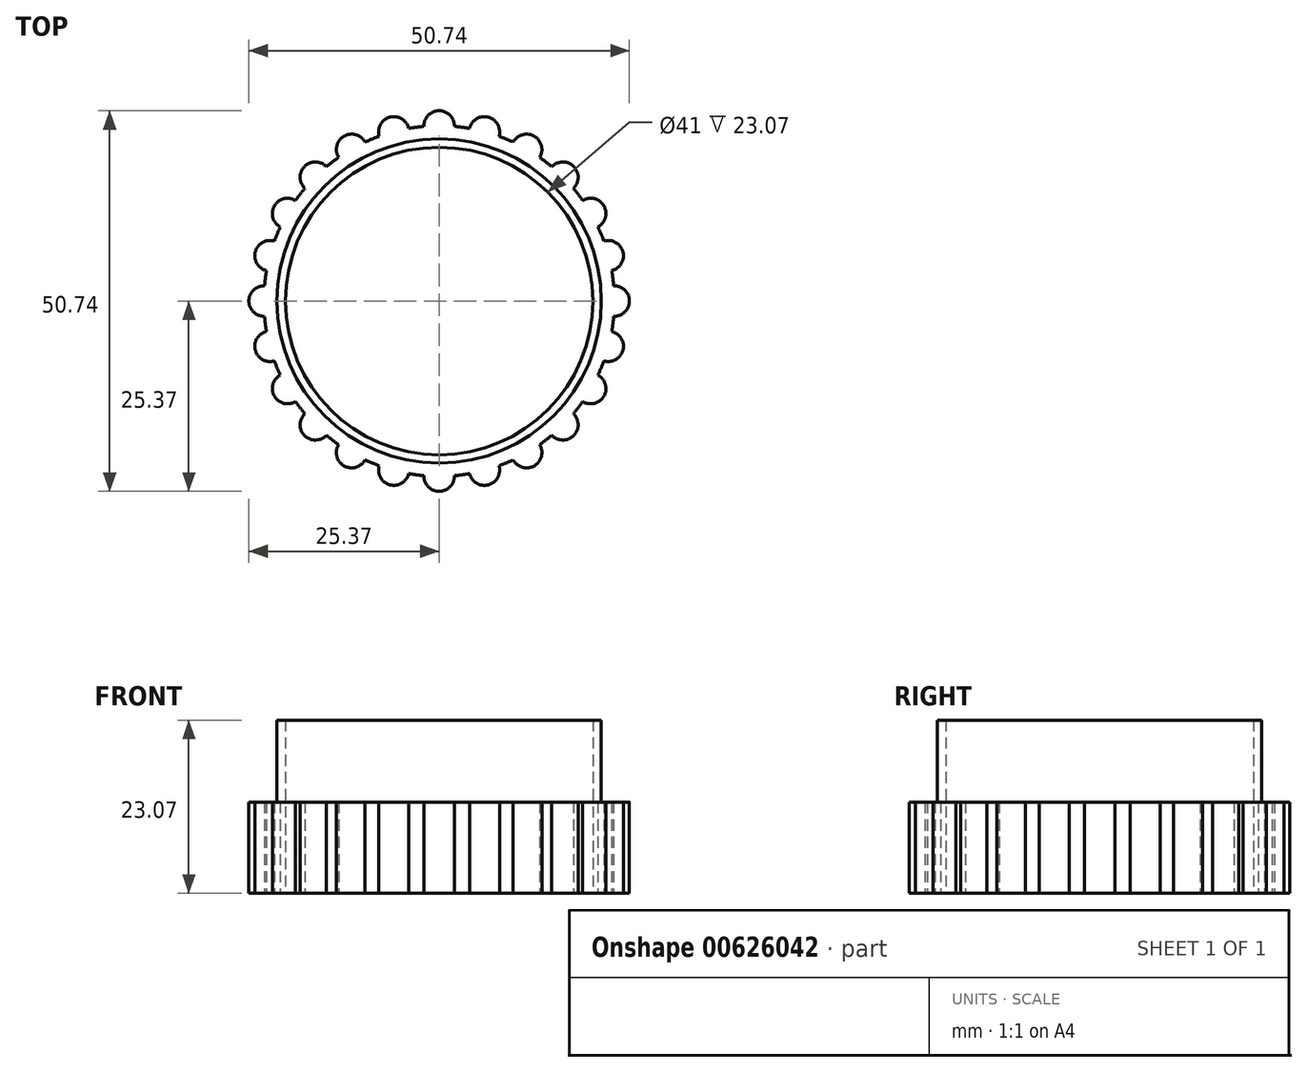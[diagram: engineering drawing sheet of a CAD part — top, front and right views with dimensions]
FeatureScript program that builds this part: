
annotation { "Feature Type Name" : "Feature", "Feature Type Description" : "" }
export const myFeature = defineFeature(function(context is Context, id is Id, definition is map)
    precondition{}
    {
        {
            var Q0;
            Q0=qCreatedBy(makeId("Front.planeOp"),FACE);
            var sketch = newSketch(context, id + "F0", { "sketchPlane" : qUnion([Q0])});
            skLineSegment(sketch, "E0", {"start": v(20.5, 0) * mm, "end": v(20.5, 23.07) * mm});
            skLineSegment(sketch, "E1", {"start": v(20.5, 23.07) * mm, "end": v(21.62, 23.07) * mm});
            skLineSegment(sketch, "E2", {"start": v(21.62, 23.07) * mm, "end": v(21.62, 12.13) * mm});
            skLineSegment(sketch, "E3", {"start": v(21.62, 12.13) * mm, "end": v(23.37, 12.13) * mm});
            skLineSegment(sketch, "E4", {"start": v(23.37, 12.13) * mm, "end": v(23.37, 0) * mm});
            skLineSegment(sketch, "E5", {"start": v(23.37, 0) * mm, "end": v(20.5, 0) * mm});
            skLineSegment(sketch, "E6", {"start": v(0, 0) * mm, "end": v(0, 12.84) * mm, "construction": true});
            skSolve(sketch);
        }
        {
            var Q0;
            Q0 = qSketchRegion(id + "F0", true);
            var Q1;
            Q1=sQuery(id+"F0.wireOp",EDGE,"E6");
            revolve(context, id + "F1", {"surfaceOperationType" : NewSurfaceOperationType.NEW, "entities" : qUnion([Q0]), "axis" : qUnion([Q1]), "revolveType" : RevolveType.FULL});
        }
        {
            var Q0;
            Q0=makeQuery(id+"F1.opRevolve","SWEPT_FACE",FACE,{"disambiguationData":[OSD([sQuery(id+"F0.wireOp",EDGE,"E5")])]});
            var sketch = newSketch(context, id + "F2", { "sketchPlane" : qUnion([Q0])});
            skCircle(sketch, "E7.0", {"center": v(0, 0) * mm, "radius": 23.37 * mm});
            skArc(sketch, "E8", {"start": v(2.03, 23.28) * mm, "mid": v(0, 25.37) * mm, "end": v(-2.03, 23.28) * mm});
            skArc(sketch, "E9.1.0", {"start": v(-4.06, 23.01) * mm, "mid": v(-6.57, 24.5) * mm, "end": v(-8, 21.96) * mm});
            skArc(sketch, "E9.2.0", {"start": v(-9.88, 21.18) * mm, "mid": v(-12.68, 21.97) * mm, "end": v(-13.4, 19.14) * mm});
            skArc(sketch, "E9.3.0", {"start": v(-15.02, 17.9) * mm, "mid": v(-17.94, 17.94) * mm, "end": v(-17.9, 15.02) * mm});
            skArc(sketch, "E9.4.0", {"start": v(-19.14, 13.4) * mm, "mid": v(-21.97, 12.68) * mm, "end": v(-21.18, 9.88) * mm});
            skArc(sketch, "E9.5.0", {"start": v(-21.96, 8) * mm, "mid": v(-24.5, 6.57) * mm, "end": v(-23.01, 4.06) * mm});
            skArc(sketch, "E9.6.0", {"start": v(-23.28, 2.04) * mm, "mid": v(-25.37, 0) * mm, "end": v(-23.28, -2.03) * mm});
            skArc(sketch, "E9.7.0", {"start": v(-23.01, -4.06) * mm, "mid": v(-24.5, -6.57) * mm, "end": v(-21.96, -8) * mm});
            skArc(sketch, "E9.8.0", {"start": v(-21.18, -9.88) * mm, "mid": v(-21.97, -12.68) * mm, "end": v(-19.14, -13.4) * mm});
            skArc(sketch, "E9.9.0", {"start": v(-17.9, -15.02) * mm, "mid": v(-17.94, -17.94) * mm, "end": v(-15.02, -17.9) * mm});
            skArc(sketch, "E9.10.0", {"start": v(-13.4, -19.14) * mm, "mid": v(-12.68, -21.97) * mm, "end": v(-9.88, -21.18) * mm});
            skArc(sketch, "E9.11.0", {"start": v(-8, -21.96) * mm, "mid": v(-6.57, -24.5) * mm, "end": v(-4.06, -23.01) * mm});
            skArc(sketch, "E9.12.0", {"start": v(-2.04, -23.28) * mm, "mid": v(0, -25.37) * mm, "end": v(2.03, -23.28) * mm});
            skArc(sketch, "E9.13.0", {"start": v(4.06, -23.01) * mm, "mid": v(6.57, -24.5) * mm, "end": v(8, -21.96) * mm});
            skArc(sketch, "E9.14.0", {"start": v(9.88, -21.18) * mm, "mid": v(12.68, -21.97) * mm, "end": v(13.4, -19.14) * mm});
            skArc(sketch, "E9.15.0", {"start": v(15.02, -17.9) * mm, "mid": v(17.94, -17.94) * mm, "end": v(17.9, -15.02) * mm});
            skArc(sketch, "E9.16.0", {"start": v(19.14, -13.4) * mm, "mid": v(21.97, -12.69) * mm, "end": v(21.18, -9.88) * mm});
            skArc(sketch, "E9.17.0", {"start": v(21.96, -8) * mm, "mid": v(24.5, -6.57) * mm, "end": v(23.01, -4.06) * mm});
            skArc(sketch, "E9.18.0", {"start": v(23.28, -2.04) * mm, "mid": v(25.37, 0) * mm, "end": v(23.28, 2.03) * mm});
            skArc(sketch, "E9.19.0", {"start": v(23.01, 4.06) * mm, "mid": v(24.5, 6.57) * mm, "end": v(21.96, 8) * mm});
            skArc(sketch, "E9.20.0", {"start": v(21.18, 9.88) * mm, "mid": v(21.97, 12.69) * mm, "end": v(19.14, 13.4) * mm});
            skArc(sketch, "E9.21.0", {"start": v(17.9, 15.02) * mm, "mid": v(17.94, 17.94) * mm, "end": v(15.02, 17.9) * mm});
            skArc(sketch, "E9.22.0", {"start": v(13.4, 19.14) * mm, "mid": v(12.69, 21.97) * mm, "end": v(9.88, 21.18) * mm});
            skArc(sketch, "E9.23.0", {"start": v(8, 21.96) * mm, "mid": v(6.57, 24.5) * mm, "end": v(4.06, 23.01) * mm});
            skSolve(sketch);
        }
        {
            var Q0;
            {var subQ0=sQuery(id+"F2.wireOp",EDGE,"E8");Q0=makeQuery(id+"F2.imprint","IMPRINT",FACE,{"disambiguationData":[TD([[makeQuery(id+"F2.imprint","IMPRINT",EDGE,{"derivedFrom":subQ0}),1.0]])]});}
            var Q1;
            {var subQ0=sQuery(id+"F2.wireOp",EDGE,"E9.1.0");Q1=makeQuery(id+"F2.imprint","IMPRINT",FACE,{"disambiguationData":[TD([[makeQuery(id+"F2.imprint","IMPRINT",EDGE,{"derivedFrom":subQ0}),1.0]])]});}
            var Q2;
            {var subQ0=sQuery(id+"F2.wireOp",EDGE,"E9.2.0");Q2=makeQuery(id+"F2.imprint","IMPRINT",FACE,{"disambiguationData":[TD([[makeQuery(id+"F2.imprint","IMPRINT",EDGE,{"derivedFrom":subQ0}),1.0]])]});}
            var Q3;
            {var subQ0=sQuery(id+"F2.wireOp",EDGE,"E9.3.0");Q3=makeQuery(id+"F2.imprint","IMPRINT",FACE,{"disambiguationData":[TD([[makeQuery(id+"F2.imprint","IMPRINT",EDGE,{"derivedFrom":subQ0}),1.0]])]});}
            var Q4;
            {var subQ0=sQuery(id+"F2.wireOp",EDGE,"E9.4.0");Q4=makeQuery(id+"F2.imprint","IMPRINT",FACE,{"disambiguationData":[TD([[makeQuery(id+"F2.imprint","IMPRINT",EDGE,{"derivedFrom":subQ0}),1.0]])]});}
            var Q5;
            {var subQ0=sQuery(id+"F2.wireOp",EDGE,"E9.5.0");Q5=makeQuery(id+"F2.imprint","IMPRINT",FACE,{"disambiguationData":[TD([[makeQuery(id+"F2.imprint","IMPRINT",EDGE,{"derivedFrom":subQ0}),1.0]])]});}
            var Q6;
            {var subQ0=sQuery(id+"F2.wireOp",EDGE,"E9.6.0");Q6=makeQuery(id+"F2.imprint","IMPRINT",FACE,{"disambiguationData":[TD([[makeQuery(id+"F2.imprint","IMPRINT",EDGE,{"derivedFrom":subQ0}),1.0]])]});}
            var Q7;
            {var subQ0=sQuery(id+"F2.wireOp",EDGE,"E9.7.0");Q7=makeQuery(id+"F2.imprint","IMPRINT",FACE,{"disambiguationData":[TD([[makeQuery(id+"F2.imprint","IMPRINT",EDGE,{"derivedFrom":subQ0}),1.0]])]});}
            var Q8;
            {var subQ0=sQuery(id+"F2.wireOp",EDGE,"E9.8.0");Q8=makeQuery(id+"F2.imprint","IMPRINT",FACE,{"disambiguationData":[TD([[makeQuery(id+"F2.imprint","IMPRINT",EDGE,{"derivedFrom":subQ0}),1.0]])]});}
            var Q9;
            {var subQ0=sQuery(id+"F2.wireOp",EDGE,"E9.9.0");Q9=makeQuery(id+"F2.imprint","IMPRINT",FACE,{"disambiguationData":[TD([[makeQuery(id+"F2.imprint","IMPRINT",EDGE,{"derivedFrom":subQ0}),1.0]])]});}
            var Q10;
            {var subQ0=sQuery(id+"F2.wireOp",EDGE,"E9.10.0");Q10=makeQuery(id+"F2.imprint","IMPRINT",FACE,{"disambiguationData":[TD([[makeQuery(id+"F2.imprint","IMPRINT",EDGE,{"derivedFrom":subQ0}),1.0]])]});}
            var Q11;
            {var subQ0=sQuery(id+"F2.wireOp",EDGE,"E9.11.0");Q11=makeQuery(id+"F2.imprint","IMPRINT",FACE,{"disambiguationData":[TD([[makeQuery(id+"F2.imprint","IMPRINT",EDGE,{"derivedFrom":subQ0}),1.0]])]});}
            var Q12;
            {var subQ0=sQuery(id+"F2.wireOp",EDGE,"E9.12.0");Q12=makeQuery(id+"F2.imprint","IMPRINT",FACE,{"disambiguationData":[TD([[makeQuery(id+"F2.imprint","IMPRINT",EDGE,{"derivedFrom":subQ0}),1.0]])]});}
            var Q13;
            {var subQ0=sQuery(id+"F2.wireOp",EDGE,"E9.13.0");Q13=makeQuery(id+"F2.imprint","IMPRINT",FACE,{"disambiguationData":[TD([[makeQuery(id+"F2.imprint","IMPRINT",EDGE,{"derivedFrom":subQ0}),1.0]])]});}
            var Q14;
            {var subQ0=sQuery(id+"F2.wireOp",EDGE,"E9.14.0");Q14=makeQuery(id+"F2.imprint","IMPRINT",FACE,{"disambiguationData":[TD([[makeQuery(id+"F2.imprint","IMPRINT",EDGE,{"derivedFrom":subQ0}),1.0]])]});}
            var Q15;
            {var subQ0=sQuery(id+"F2.wireOp",EDGE,"E9.15.0");Q15=makeQuery(id+"F2.imprint","IMPRINT",FACE,{"disambiguationData":[TD([[makeQuery(id+"F2.imprint","IMPRINT",EDGE,{"derivedFrom":subQ0}),1.0]])]});}
            var Q16;
            {var subQ0=sQuery(id+"F2.wireOp",EDGE,"E9.16.0");Q16=makeQuery(id+"F2.imprint","IMPRINT",FACE,{"disambiguationData":[TD([[makeQuery(id+"F2.imprint","IMPRINT",EDGE,{"derivedFrom":subQ0}),1.0]])]});}
            var Q17;
            {var subQ0=sQuery(id+"F2.wireOp",EDGE,"E9.17.0");Q17=makeQuery(id+"F2.imprint","IMPRINT",FACE,{"disambiguationData":[TD([[makeQuery(id+"F2.imprint","IMPRINT",EDGE,{"derivedFrom":subQ0}),1.0]])]});}
            var Q18;
            {var subQ0=sQuery(id+"F2.wireOp",EDGE,"E9.18.0");Q18=makeQuery(id+"F2.imprint","IMPRINT",FACE,{"disambiguationData":[TD([[makeQuery(id+"F2.imprint","IMPRINT",EDGE,{"derivedFrom":subQ0}),1.0]])]});}
            var Q19;
            {var subQ0=sQuery(id+"F2.wireOp",EDGE,"E9.19.0");Q19=makeQuery(id+"F2.imprint","IMPRINT",FACE,{"disambiguationData":[TD([[makeQuery(id+"F2.imprint","IMPRINT",EDGE,{"derivedFrom":subQ0}),1.0]])]});}
            var Q20;
            {var subQ0=sQuery(id+"F2.wireOp",EDGE,"E9.20.0");Q20=makeQuery(id+"F2.imprint","IMPRINT",FACE,{"disambiguationData":[TD([[makeQuery(id+"F2.imprint","IMPRINT",EDGE,{"derivedFrom":subQ0}),1.0]])]});}
            var Q21;
            {var subQ0=sQuery(id+"F2.wireOp",EDGE,"E9.21.0");Q21=makeQuery(id+"F2.imprint","IMPRINT",FACE,{"disambiguationData":[TD([[makeQuery(id+"F2.imprint","IMPRINT",EDGE,{"derivedFrom":subQ0}),1.0]])]});}
            var Q22;
            {var subQ0=sQuery(id+"F2.wireOp",EDGE,"E9.22.0");Q22=makeQuery(id+"F2.imprint","IMPRINT",FACE,{"disambiguationData":[TD([[makeQuery(id+"F2.imprint","IMPRINT",EDGE,{"derivedFrom":subQ0}),1.0]])]});}
            var Q23;
            {var subQ0=sQuery(id+"F2.wireOp",EDGE,"E9.23.0");Q23=makeQuery(id+"F2.imprint","IMPRINT",FACE,{"disambiguationData":[TD([[makeQuery(id+"F2.imprint","IMPRINT",EDGE,{"derivedFrom":subQ0}),1.0]])]});}
            extrude(context, id + "F3", {"entities" : qUnion([Q0, Q1, Q2, Q3, Q4, Q5, Q6, Q7, Q8, Q9, Q10, Q11, Q12, Q13, Q14, Q15, Q16, Q17, Q18, Q19, Q20, Q21, Q22, Q23]), "operationType" : NewBodyOperationType.ADD, "oppositeDirection" : true, "depth" : 12.13 * mm, "offsetDistance" : 25 * mm});
        }
    });
